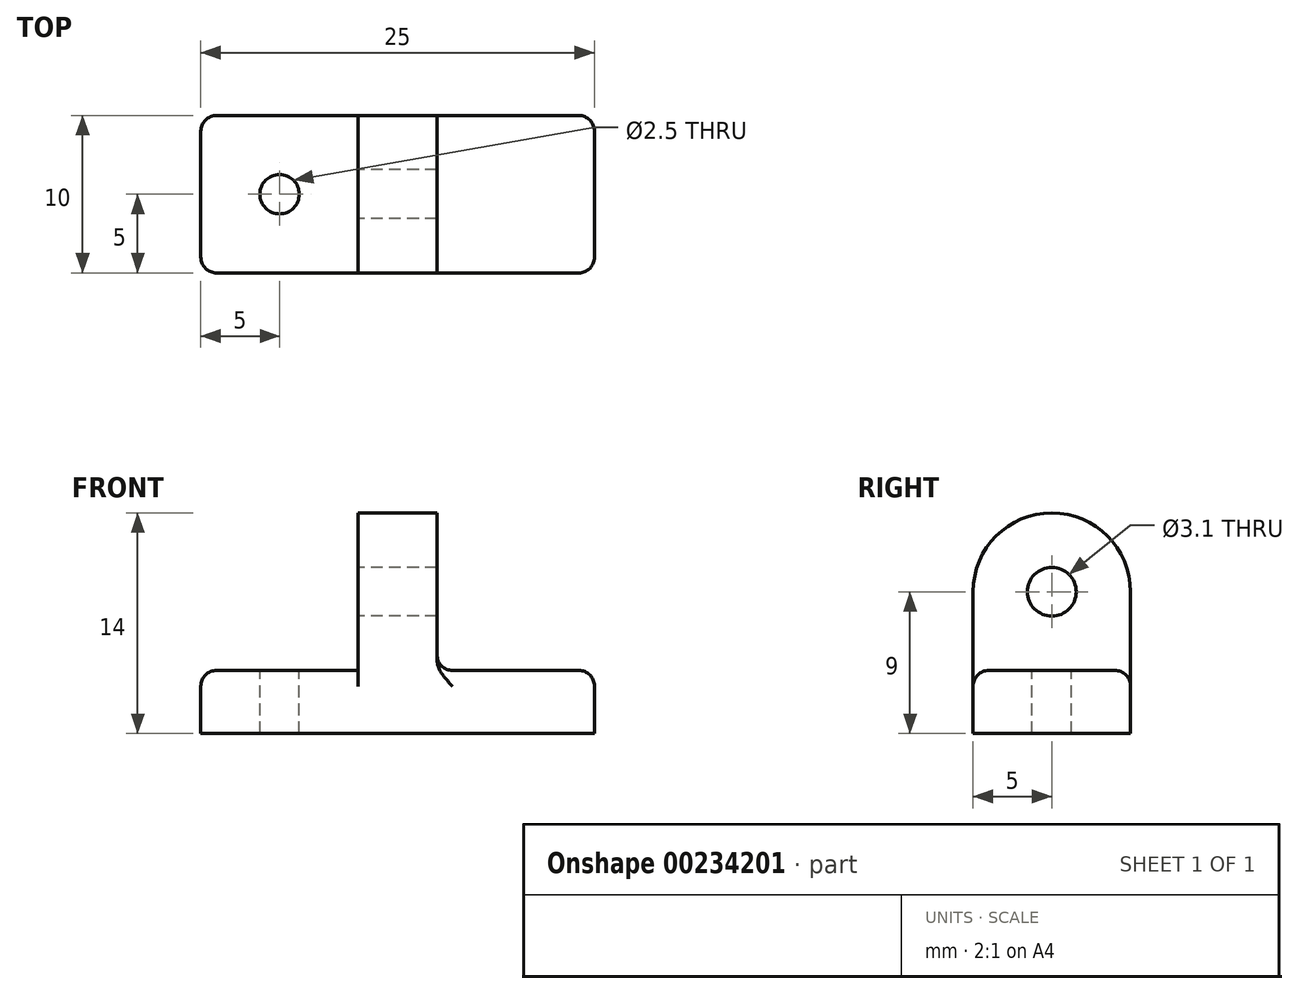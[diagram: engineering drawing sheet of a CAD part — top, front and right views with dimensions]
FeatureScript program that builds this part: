
annotation { "Feature Type Name" : "Feature", "Feature Type Description" : "" }
export const myFeature = defineFeature(function(context is Context, id is Id, definition is map)
    precondition{}
    {
        {
            var Q0;
            Q0=qCreatedBy(makeId("Top.planeOp"),FACE);
            var sketch = newSketch(context, id + "F0", { "sketchPlane" : qUnion([Q0])});
            skLineSegment(sketch, "E0.bottom", {"start": v(12.5, 5) * mm, "end": v(-12.5, 5) * mm});
            skLineSegment(sketch, "E0.top", {"start": v(12.5, -5) * mm, "end": v(-12.5, -5) * mm});
            skLineSegment(sketch, "E0.left", {"start": v(12.5, 5) * mm, "end": v(12.5, -5) * mm});
            skLineSegment(sketch, "E0.right", {"start": v(-12.5, 5) * mm, "end": v(-12.5, -5) * mm});
            skPoint(sketch, "E0.middle", {"position": v(0, 0) * mm});
            skSolve(sketch);
        }
        {
            var Q0;
            Q0=qSketchRegion(id+"F0",true);
            extrude(context, id + "F1", {"entities" : qUnion([Q0]), "depth" : 4 * mm});
        }
        {
            var Q0;
            Q0=makeQuery(id+"F1.opExtrude","CAP_FACE",FACE,{"disambiguationData":[OSD([sQuery(id+"F0.wireOp",EDGE,"E0.bottom"),sQuery(id+"F0.wireOp",EDGE,"E0.top"),sQuery(id+"F0.wireOp",EDGE,"E0.left"),sQuery(id+"F0.wireOp",EDGE,"E0.right")])],"isStart":false});
            var sketch = newSketch(context, id + "F2", { "sketchPlane" : qUnion([Q0])});
            skLineSegment(sketch, "E1.bottom", {"start": v(2.5, 5) * mm, "end": v(-2.5, 5) * mm});
            skLineSegment(sketch, "E1.top", {"start": v(2.5, -5) * mm, "end": v(-2.5, -5) * mm});
            skLineSegment(sketch, "E1.left", {"start": v(2.5, 5) * mm, "end": v(2.5, -5) * mm});
            skLineSegment(sketch, "E1.right", {"start": v(-2.5, 5) * mm, "end": v(-2.5, -5) * mm});
            skPoint(sketch, "E1.middle", {"position": v(0, 0) * mm});
            skSolve(sketch);
        }
        {
            var Q0;
            Q0=qSketchRegion(id+"F2",true);
            extrude(context, id + "F3", {"entities" : qUnion([Q0]), "operationType" : NewBodyOperationType.ADD, "depth" : 10 * mm});
        }
        {
            var Q0;
            {var subQ0=sQuery(id+"F0.wireOp",EDGE,"E0.right");var subQ1=sQuery(id+"F0.wireOp",EDGE,"E0.top");var subQ2=sQuery(id+"F0.wireOp",EDGE,"E0.bottom");Q0=makeQuery(id+"F3.boolean.opBoolean","SPLIT",FACE,{"disambiguationData":[TD([makeQuery(id+"F1.opExtrude","SWEPT_FACE",FACE,{"disambiguationData":[OSD([subQ0])]})])],"derivedFrom":makeQuery(id+"F1.opExtrude","CAP_FACE",FACE,{"disambiguationData":[OSD([subQ2,subQ1,sQuery(id+"F0.wireOp",EDGE,"E0.left"),subQ0])],"isStart":false})});}
            var sketch = newSketch(context, id + "F4", { "sketchPlane" : qUnion([Q0])});
            skCircle(sketch, "E2", {"center": v(-7.5, 0) * mm, "radius": 1.25 * mm});
            skLineSegment(sketch, "E3", {"start": v(-12.5, 5) * mm, "end": v(-2.5, -5) * mm, "construction": true});
            skSolve(sketch);
        }
        {
            var Q0;
            Q0=qSketchRegion(id+"F4",true);
            extrude(context, id + "F5", {"entities" : qUnion([Q0]), "operationType" : NewBodyOperationType.REMOVE, "endBound" : BoundingType.THROUGH_ALL, "oppositeDirection" : true, "depth" : 25 * mm});
        }
        {
            var Q0;
            {var subQ0=sQuery(id+"F0.wireOp",EDGE,"E0.right");var subQ1=sQuery(id+"F0.wireOp",EDGE,"E0.top");var subQ2=sQuery(id+"F0.wireOp",EDGE,"E0.bottom");Q0=makeQuery(id+"F3.boolean.opBoolean","SPLIT",FACE,{"disambiguationData":[TD([makeQuery(id+"F1.opExtrude","SWEPT_FACE",FACE,{"disambiguationData":[OSD([subQ0])]})])],"derivedFrom":makeQuery(id+"F1.opExtrude","CAP_FACE",FACE,{"disambiguationData":[OSD([subQ2,subQ1,sQuery(id+"F0.wireOp",EDGE,"E0.left"),subQ0])],"isStart":false})});}
            var sketch = newSketch(context, id + "F6", { "sketchPlane" : qUnion([Q0])});
            skLineSegment(sketch, "E4", {"start": v(-2.5, -5) * mm, "end": v(-12.5, 5) * mm, "construction": true});
            skCircle(sketch, "E5", {"center": v(-7.5, 0) * mm, "radius": 3 * mm});
            skSolve(sketch);
        }
        {
            var Q0;
            Q0=makeQuery(id+"F3.opExtrude","CAP_EDGE",EDGE,{"disambiguationData":[OSD([sQuery(id+"F2.wireOp",EDGE,"E1.top")])],"isStart":false});
            var Q1;
            Q1=makeQuery(id+"F3.opExtrude","CAP_EDGE",EDGE,{"disambiguationData":[OSD([sQuery(id+"F2.wireOp",EDGE,"E1.bottom")])],"isStart":false});
            fillet(context, id + "F7", {"entities" : qUnion([Q0, Q1]), "radius" : 5 * mm, "tangentPropagation" : true, "allowEdgeOverflow" : false});
        }
        {
            var Q0;
            Q0=makeQuery(id+"F3.opExtrude","SWEPT_FACE",FACE,{"disambiguationData":[OSD([sQuery(id+"F2.wireOp",EDGE,"E1.right")])]});
            var sketch = newSketch(context, id + "F8", { "sketchPlane" : qUnion([Q0])});
            skLineSegment(sketch, "E6", {"start": v(5, 9) * mm, "end": v(-5, 9) * mm, "construction": true});
            skCircle(sketch, "E7", {"center": v(0, 9) * mm, "radius": 1.55 * mm});
            skSolve(sketch);
        }
        {
            var Q0;
            Q0=qSketchRegion(id+"F8",true);
            extrude(context, id + "F9", {"entities" : qUnion([Q0]), "operationType" : NewBodyOperationType.REMOVE, "endBound" : BoundingType.THROUGH_ALL, "oppositeDirection" : true, "depth" : 25 * mm});
        }
        {
            var Q0;
            {var subQ0=sQuery(id+"F0.wireOp",EDGE,"E0.left");var subQ1=sQuery(id+"F0.wireOp",EDGE,"E0.top");Q0=makeQuery(id+"F3.boolean.opBoolean","SPLIT",EDGE,{"disambiguationData":[TD([makeQuery(id+"F1.opExtrude","SWEPT_FACE",FACE,{"disambiguationData":[OSD([subQ0])]})])],"derivedFrom":makeQuery(id+"F1.opExtrude","CAP_EDGE",EDGE,{"disambiguationData":[OSD([subQ1])],"isStart":false})});}
            var Q1;
            Q1=makeQuery(id+"F1.opExtrude","CAP_EDGE",EDGE,{"disambiguationData":[OSD([sQuery(id+"F0.wireOp",EDGE,"E0.left")])],"isStart":false});
            var Q2;
            {var subQ0=sQuery(id+"F0.wireOp",EDGE,"E0.left");var subQ1=sQuery(id+"F0.wireOp",EDGE,"E0.bottom");Q2=makeQuery(id+"F3.boolean.opBoolean","SPLIT",EDGE,{"disambiguationData":[TD([makeQuery(id+"F1.opExtrude","SWEPT_FACE",FACE,{"disambiguationData":[OSD([subQ0])]})])],"derivedFrom":makeQuery(id+"F1.opExtrude","CAP_EDGE",EDGE,{"disambiguationData":[OSD([subQ1])],"isStart":false})});}
            var Q3;
            Q3=makeQuery(id+"F1.opExtrude","SWEPT_EDGE",EDGE,{"disambiguationData":[OSD([sQuery(id+"F0.wireOp",EDGE,"E0.top"),sQuery(id+"F0.wireOp",EDGE,"E0.left")])]});
            var Q4;
            Q4=makeQuery(id+"F1.opExtrude","SWEPT_EDGE",EDGE,{"disambiguationData":[OSD([sQuery(id+"F0.wireOp",EDGE,"E0.bottom"),sQuery(id+"F0.wireOp",EDGE,"E0.left")])]});
            var Q5;
            Q5=makeQuery(id+"F1.opExtrude","SWEPT_EDGE",EDGE,{"disambiguationData":[OSD([sQuery(id+"F0.wireOp",EDGE,"E0.top"),sQuery(id+"F0.wireOp",EDGE,"E0.right")])]});
            var Q6;
            Q6=makeQuery(id+"F1.opExtrude","SWEPT_EDGE",EDGE,{"disambiguationData":[OSD([sQuery(id+"F0.wireOp",EDGE,"E0.bottom"),sQuery(id+"F0.wireOp",EDGE,"E0.right")])]});
            var Q7;
            Q7=makeQuery(id+"F1.opExtrude","CAP_EDGE",EDGE,{"disambiguationData":[OSD([sQuery(id+"F0.wireOp",EDGE,"E0.right")])],"isStart":false});
            var Q8;
            {var subQ0=sQuery(id+"F0.wireOp",EDGE,"E0.right");var subQ1=sQuery(id+"F0.wireOp",EDGE,"E0.top");Q8=makeQuery(id+"F3.boolean.opBoolean","SPLIT",EDGE,{"disambiguationData":[TD([makeQuery(id+"F1.opExtrude","SWEPT_FACE",FACE,{"disambiguationData":[OSD([subQ0])]})])],"derivedFrom":makeQuery(id+"F1.opExtrude","CAP_EDGE",EDGE,{"disambiguationData":[OSD([subQ1])],"isStart":false})});}
            var Q9;
            {var subQ0=sQuery(id+"F0.wireOp",EDGE,"E0.right");var subQ1=sQuery(id+"F0.wireOp",EDGE,"E0.bottom");Q9=makeQuery(id+"F3.boolean.opBoolean","SPLIT",EDGE,{"disambiguationData":[TD([makeQuery(id+"F1.opExtrude","SWEPT_FACE",FACE,{"disambiguationData":[OSD([subQ0])]})])],"derivedFrom":makeQuery(id+"F1.opExtrude","CAP_EDGE",EDGE,{"disambiguationData":[OSD([subQ1])],"isStart":false})});}
            fillet(context, id + "F10", {"entities" : qUnion([Q0, Q1, Q2, Q3, Q4, Q5, Q6, Q7, Q8, Q9]), "radius" : 1 * mm, "tangentPropagation" : true, "allowEdgeOverflow" : false});
        }
        {
            var Q0;
            Q0=makeQuery(id+"F3.opExtrude","CAP_EDGE",EDGE,{"disambiguationData":[OSD([sQuery(id+"F2.wireOp",EDGE,"E1.left")])],"isStart":true});
            var Q1;
            Q1=makeQuery(id+"F3.opExtrude","CAP_EDGE",EDGE,{"disambiguationData":[OSD([sQuery(id+"F2.wireOp",EDGE,"E1.right")])],"isStart":true});
            fillet(context, id + "F11", {"entities" : qUnion([Q0, Q1]), "radius" : 1 * mm, "tangentPropagation" : true, "allowEdgeOverflow" : false});
        }
    });
